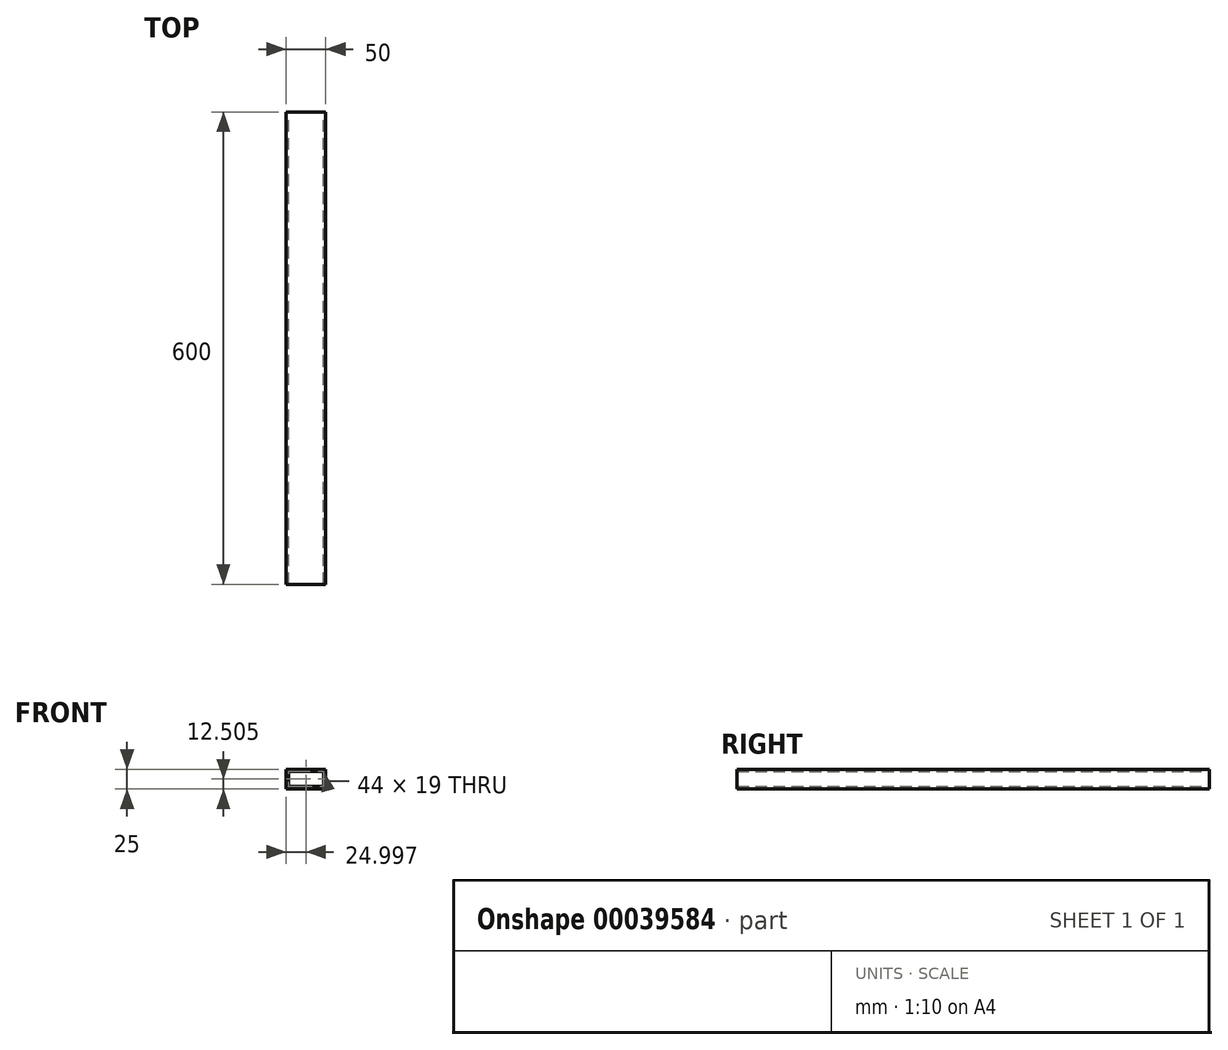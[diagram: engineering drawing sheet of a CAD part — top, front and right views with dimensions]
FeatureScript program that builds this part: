
annotation { "Feature Type Name" : "Feature", "Feature Type Description" : "" }
export const myFeature = defineFeature(function(context is Context, id is Id, definition is map)
    precondition{}
    {
        {
            var Q0;
            Q0=qCreatedBy(makeId("Front.planeOp"),FACE);
            var sketch = newSketch(context, id + "F0", { "sketchPlane" : qUnion([Q0])});
            skLineSegment(sketch, "E0.bottom", {"start": v(-57.78, 50.37) * mm, "end": v(-7.78, 50.37) * mm});
            skLineSegment(sketch, "E0.top", {"start": v(-57.78, 25.37) * mm, "end": v(-7.78, 25.37) * mm});
            skLineSegment(sketch, "E0.left", {"start": v(-57.78, 50.37) * mm, "end": v(-57.78, 25.37) * mm});
            skLineSegment(sketch, "E0.right", {"start": v(-7.78, 50.37) * mm, "end": v(-7.78, 25.37) * mm});
            skLineSegment(sketch, "E1.bottom", {"start": v(-54.78, 47.37) * mm, "end": v(-10.78, 47.37) * mm});
            skLineSegment(sketch, "E1.top", {"start": v(-54.78, 28.37) * mm, "end": v(-10.78, 28.37) * mm});
            skLineSegment(sketch, "E1.left", {"start": v(-54.78, 47.37) * mm, "end": v(-54.78, 28.37) * mm});
            skLineSegment(sketch, "E1.right", {"start": v(-10.78, 47.37) * mm, "end": v(-10.78, 28.37) * mm});
            skSolve(sketch);
        }
        {
            var Q0;
            Q0 = qSketchRegion(id + "F0", true);
            extrude(context, id + "F1", {"entities" : qUnion([Q0]), "depth" : 600 * mm});
        }
    });
